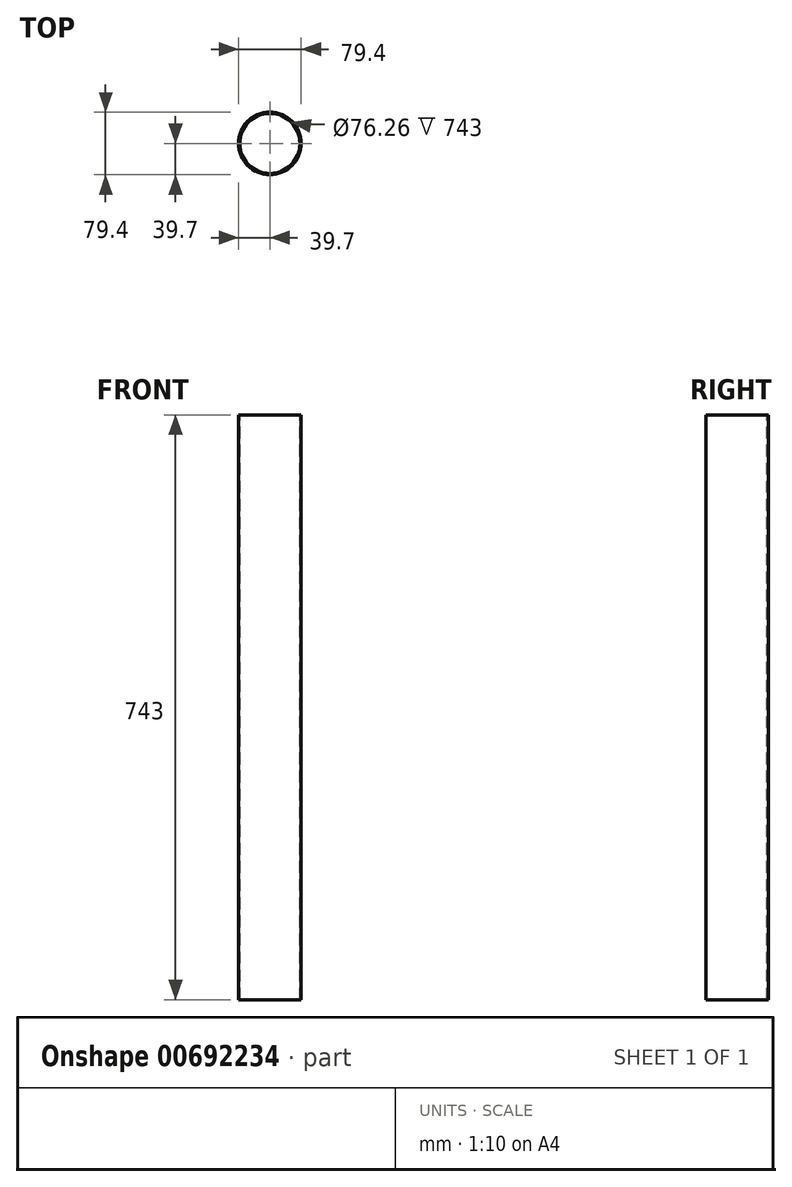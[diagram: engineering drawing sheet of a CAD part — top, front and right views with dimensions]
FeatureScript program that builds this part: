
annotation { "Feature Type Name" : "Feature", "Feature Type Description" : "" }
export const myFeature = defineFeature(function(context is Context, id is Id, definition is map)
    precondition{}
    {
        {
            var Q0;
            Q0=qCreatedBy(makeId("Front.planeOp"),FACE);
            var sketch = newSketch(context, id + "F0", { "sketchPlane" : qUnion([Q0])});
            skLineSegment(sketch, "E0", {"start": v(-39.7, 0) * mm, "end": v(-39.7, 743) * mm});
            skLineSegment(sketch, "E1", {"start": v(-39.7, 743) * mm, "end": v(-38.13, 743) * mm});
            skLineSegment(sketch, "E2", {"start": v(-38.13, 743) * mm, "end": v(-38.13, 0) * mm});
            skLineSegment(sketch, "E3", {"start": v(-38.13, 0) * mm, "end": v(-39.7, 0) * mm});
            skLineSegment(sketch, "E4", {"start": v(0, 0) * mm, "end": v(0, -40.56) * mm});
            skSolve(sketch);
        }
        {
            var Q0;
            Q0 = qSketchRegion(id + "F0", true);
            var Q1;
            Q1=sQuery(id+"F0.wireOp",EDGE,"E4");
            revolve(context, id + "F1", {"surfaceOperationType" : NewSurfaceOperationType.NEW, "entities" : qUnion([Q0]), "axis" : qUnion([Q1]), "revolveType" : RevolveType.FULL});
        }
    });
